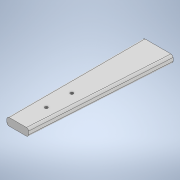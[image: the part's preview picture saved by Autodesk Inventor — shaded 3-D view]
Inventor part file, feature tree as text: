
AUTODESK INVENTOR PART (.ipt)
format: ipt  version: 2020 (Build 240168000, 168)  size: 114,176 bytes
history: native  units: mm
features: sketch x2, extrude x1, hole x1, fillet x1
ambient origin geometry x8: Origin, YZ Plane, XZ Plane, XY Plane, X Axis, Y Axis, Z Axis, Center Point
bodies: Volumenkörper1 (feature_tree)
feature tree (5):
  extrude  "Extrusion1"  Depth=65.0mm
  hole  "Bohrung1"  [1 undecoded]
  fillet  "Rundung1"  Radius=13.0mm
  sketch  "Skizze1"  dims[d0=65.0mm d1=14.4mm]
  sketch  "Skizze2"  dims[d2=10.3mm d3=3.6mm d4=0.0mm d5=13.0mm d6=25.0mm d7=5.8mm d8=6.0mm d9=1.4mm d10=6.0mm d11=4.0mm d12=2.0mm d13=90.0deg d14=8.0mm d15=20.594885mm d16=1.0mm]
note: 1 required parameter value undecoded (feature->parameter linkage not recoverable at this tier; creation-order binding heuristic only, values carry confidence <= 0.55)
